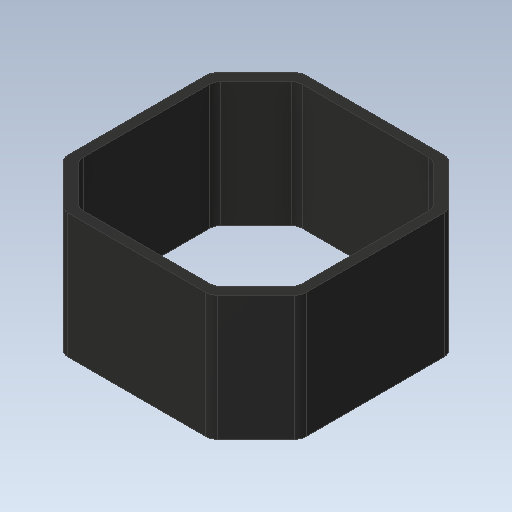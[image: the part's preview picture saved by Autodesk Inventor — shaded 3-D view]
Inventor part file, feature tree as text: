
AUTODESK INVENTOR PART (.ipt)
format: ipt  version: 2020 (Build 240168000, 168)  size: 180,224 bytes
history: native  units: mm
features: sketch x4, extrude x3, fillet x2, chamfer x1, projected_geometry x1
ambient origin geometry x8: Origin, YZ Plane, XZ Plane, XY Plane, X Axis, Y Axis, Z Axis, Center Point
bodies: Solid1 (feature_tree)
feature tree (11):
  extrude  "Extrusion1"  Depth=42.0mm
  chamfer  "Chamfer1"  Distance=22.0mm
  fillet  "Fillet1"  Radius=2.0mm
  extrude  "Extrusion2"  Depth=20.0mm
  extrude  "Extrusion3"  Depth=10.0mm
  sketch  "Sketch6"  dims[d19=10.0mm d20=10.0mm d21=0.001mm d22=0.0mm d23=2.0mm]
  fillet  "Fillet2"  Radius=0.001mm
  sketch  "Sketch1"  dims[d0=42.0mm d1=42.0mm d2=22.0mm d3=0.0mm]
  sketch  "Sketch4"  dims[d4=8.0mm d5=2.0mm d6=45.0deg d7=2.0mm]
  projected_geometry  "Projected Loop2"
  sketch  "Sketch5"  dims[d8=22.0mm d9=0.0mm d18=20.0mm]
